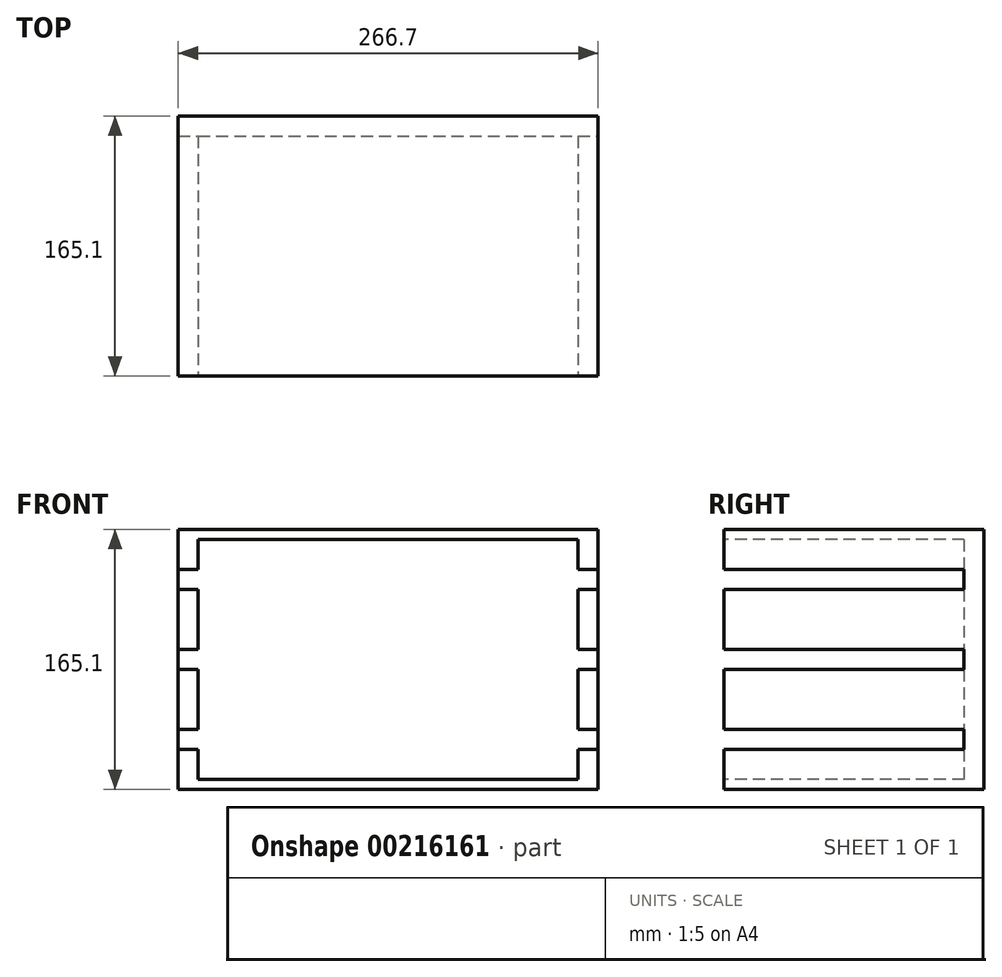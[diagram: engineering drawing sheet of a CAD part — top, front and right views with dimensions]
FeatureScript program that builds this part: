
annotation { "Feature Type Name" : "Feature", "Feature Type Description" : "" }
export const myFeature = defineFeature(function(context is Context, id is Id, definition is map)
    precondition{}
    {
        {
            var Q0;
            Q0=qCreatedBy(makeId("Front.planeOp"),FACE);
            var sketch = newSketch(context, id + "F0", { "sketchPlane" : qUnion([Q0])});
            skLineSegment(sketch, "E0.bottom", {"start": v(-150.4, 80.77) * mm, "end": v(116.3, 80.77) * mm});
            skLineSegment(sketch, "E0.top", {"start": v(-150.4, -84.33) * mm, "end": v(116.3, -84.33) * mm});
            skLineSegment(sketch, "E0.left", {"start": v(-150.4, 80.77) * mm, "end": v(-150.4, -84.33) * mm});
            skLineSegment(sketch, "E0.right", {"start": v(116.3, 80.77) * mm, "end": v(116.3, -84.33) * mm});
            skSolve(sketch);
        }
        {
            var Q0;
            Q0=makeQuery(id+"F0.imprint","IMPRINT",FACE,{"disambiguationData":[TD([[makeQuery(id+"F0.imprint","IMPRINT",EDGE,{"derivedFrom":sQuery(id+"F0.wireOp",EDGE,"E0.bottom")}),-1.0]])]});
            extrude(context, id + "F1", {"entities" : qUnion([Q0]), "oppositeDirection" : true, "depth" : 165.1 * mm});
        }
        {
            var Q0;
            Q0=makeQuery(id+"F1.opExtrude","CAP_FACE",FACE,{"disambiguationData":[OSD([sQuery(id+"F0.wireOp",EDGE,"E0.bottom"),sQuery(id+"F0.wireOp",EDGE,"E0.top"),sQuery(id+"F0.wireOp",EDGE,"E0.left"),sQuery(id+"F0.wireOp",EDGE,"E0.right")])],"isStart":true});
            var sketch = newSketch(context, id + "F2", { "sketchPlane" : qUnion([Q0])});
            skLineSegment(sketch, "E1.bottom", {"start": v(-137.7, 74.42) * mm, "end": v(103.6, 74.42) * mm});
            skLineSegment(sketch, "E1.top", {"start": v(-137.7, -77.98) * mm, "end": v(103.6, -77.98) * mm});
            skLineSegment(sketch, "E1.left", {"start": v(-137.7, 74.42) * mm, "end": v(-137.7, -77.98) * mm});
            skLineSegment(sketch, "E1.right", {"start": v(103.6, 74.42) * mm, "end": v(103.6, -77.98) * mm});
            skSolve(sketch);
        }
        {
            var Q0;
            Q0=makeQuery(id+"F2.imprint","IMPRINT",FACE,{"disambiguationData":[TD([[makeQuery(id+"F2.imprint","IMPRINT",EDGE,{"derivedFrom":sQuery(id+"F2.wireOp",EDGE,"E1.bottom")}),-1.0]])]});
            extrude(context, id + "F3", {"entities" : qUnion([Q0]), "operationType" : NewBodyOperationType.REMOVE, "oppositeDirection" : true, "depth" : 152.4 * mm});
        }
        {
            var Q0;
            Q0=makeQuery(id+"F1.opExtrude","CAP_FACE",FACE,{"disambiguationData":[OSD([sQuery(id+"F0.wireOp",EDGE,"E0.bottom"),sQuery(id+"F0.wireOp",EDGE,"E0.top"),sQuery(id+"F0.wireOp",EDGE,"E0.left"),sQuery(id+"F0.wireOp",EDGE,"E0.right")])],"isStart":true});
            var sketch = newSketch(context, id + "F4", { "sketchPlane" : qUnion([Q0])});
            skLineSegment(sketch, "E2.bottom", {"start": v(-150.4, -46.23) * mm, "end": v(-137.7, -46.23) * mm});
            skLineSegment(sketch, "E2.top", {"start": v(-150.4, -58.93) * mm, "end": v(-137.7, -58.93) * mm});
            skLineSegment(sketch, "E2.left", {"start": v(-150.4, -46.23) * mm, "end": v(-150.4, -58.93) * mm});
            skLineSegment(sketch, "E2.right", {"start": v(-137.7, -46.23) * mm, "end": v(-137.7, -58.93) * mm});
            skLineSegment(sketch, "E3.bottom", {"start": v(-150.4, 4.57) * mm, "end": v(-137.7, 4.57) * mm});
            skLineSegment(sketch, "E3.top", {"start": v(-150.4, -8.13) * mm, "end": v(-137.7, -8.13) * mm});
            skLineSegment(sketch, "E3.left", {"start": v(-150.4, 4.57) * mm, "end": v(-150.4, -8.13) * mm});
            skLineSegment(sketch, "E3.right", {"start": v(-137.7, 4.57) * mm, "end": v(-137.7, -8.13) * mm});
            skLineSegment(sketch, "E4.bottom", {"start": v(-150.4, 55.37) * mm, "end": v(-137.7, 55.37) * mm});
            skLineSegment(sketch, "E4.top", {"start": v(-150.4, 42.67) * mm, "end": v(-137.7, 42.67) * mm});
            skLineSegment(sketch, "E4.left", {"start": v(-150.4, 55.37) * mm, "end": v(-150.4, 42.67) * mm});
            skLineSegment(sketch, "E4.right", {"start": v(-137.7, 55.37) * mm, "end": v(-137.7, 42.67) * mm});
            skLineSegment(sketch, "E5.bottom", {"start": v(103.6, -46.23) * mm, "end": v(116.3, -46.23) * mm});
            skLineSegment(sketch, "E5.top", {"start": v(103.6, -58.93) * mm, "end": v(116.3, -58.93) * mm});
            skLineSegment(sketch, "E5.left", {"start": v(103.6, -46.23) * mm, "end": v(103.6, -58.93) * mm});
            skLineSegment(sketch, "E5.right", {"start": v(116.3, -46.23) * mm, "end": v(116.3, -58.93) * mm});
            skLineSegment(sketch, "E6.bottom", {"start": v(103.6, 4.57) * mm, "end": v(116.3, 4.57) * mm});
            skLineSegment(sketch, "E6.top", {"start": v(103.6, -8.13) * mm, "end": v(116.3, -8.13) * mm});
            skLineSegment(sketch, "E6.left", {"start": v(103.6, 4.57) * mm, "end": v(103.6, -8.13) * mm});
            skLineSegment(sketch, "E6.right", {"start": v(116.3, 4.57) * mm, "end": v(116.3, -8.13) * mm});
            skLineSegment(sketch, "E7.bottom", {"start": v(103.6, 55.37) * mm, "end": v(116.3, 55.37) * mm});
            skLineSegment(sketch, "E7.top", {"start": v(103.6, 42.67) * mm, "end": v(116.3, 42.67) * mm});
            skLineSegment(sketch, "E7.left", {"start": v(103.6, 55.37) * mm, "end": v(103.6, 42.67) * mm});
            skLineSegment(sketch, "E7.right", {"start": v(116.3, 55.37) * mm, "end": v(116.3, 42.67) * mm});
            skSolve(sketch);
        }
        {
            var Q0;
            Q0 = qSketchRegion(id + "F4", true);
            extrude(context, id + "F5", {"entities" : qUnion([Q0]), "operationType" : NewBodyOperationType.REMOVE, "oppositeDirection" : true, "depth" : 152.4 * mm});
        }
    });
